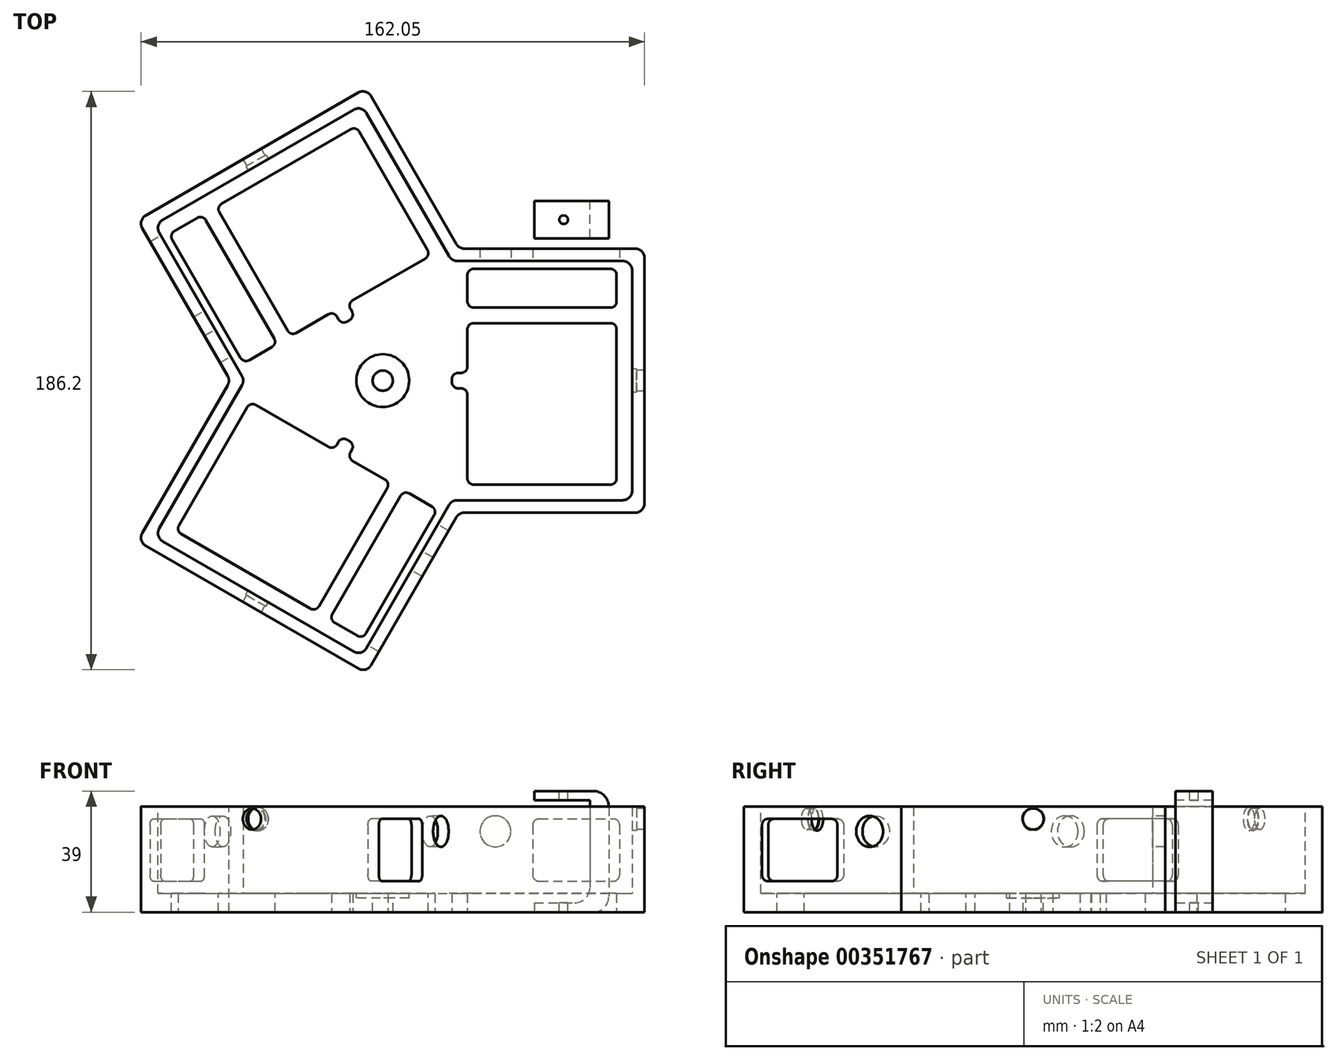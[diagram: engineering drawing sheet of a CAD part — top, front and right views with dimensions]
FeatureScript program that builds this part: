
annotation { "Feature Type Name" : "Feature", "Feature Type Description" : "" }
export const myFeature = defineFeature(function(context is Context, id is Id, definition is map)
    precondition{}
    {
        {
            var Q0;
            Q0=qCreatedBy(makeId("Top.planeOp"),FACE);
            var sketch = newSketch(context, id + "F0", { "sketchPlane" : qUnion([Q0])});
            skCircle(sketch, "E0.cCircle", {"center": v(0, 0) * mm, "radius": 22.23 * mm, "construction": true});
            skLineSegment(sketch, "E0.0", {"start": v(22.23, 38.5) * mm, "end": v(22.23, -38.5) * mm});
            skLineSegment(sketch, "E0.1", {"start": v(22.23, -38.5) * mm, "end": v(-44.46, 0) * mm});
            skLineSegment(sketch, "E0.2", {"start": v(-44.46, 0) * mm, "end": v(22.23, 38.5) * mm});
            skPoint(sketch, "E0.0.midPoint", {"position": v(22.23, 0) * mm});
            skLineSegment(sketch, "E1.bottom", {"start": v(22.23, 38.5) * mm, "end": v(80.23, 38.5) * mm});
            skLineSegment(sketch, "E1.top", {"start": v(22.23, -38.5) * mm, "end": v(80.23, -38.5) * mm});
            skLineSegment(sketch, "E1.right", {"start": v(80.23, 38.5) * mm, "end": v(80.23, -38.5) * mm});
            skLineSegment(sketch, "E2", {"start": v(22.23, 38.5) * mm, "end": v(-6.77, 88.73) * mm});
            skLineSegment(sketch, "E3", {"start": v(-6.77, 88.73) * mm, "end": v(-73.46, 50.23) * mm});
            skLineSegment(sketch, "E4", {"start": v(-73.46, 50.23) * mm, "end": v(-44.46, 0) * mm});
            skLineSegment(sketch, "E5", {"start": v(-44.46, 0) * mm, "end": v(-73.46, -50.23) * mm});
            skLineSegment(sketch, "E6", {"start": v(-73.46, -50.23) * mm, "end": v(-6.77, -88.73) * mm});
            skLineSegment(sketch, "E7", {"start": v(-6.77, -88.73) * mm, "end": v(22.23, -38.5) * mm});
            skLineSegment(sketch, "E8.0", {"start": v(24.54, 42.5) * mm, "end": v(-5.3, 94.2) * mm});
            skLineSegment(sketch, "E8.1", {"start": v(-5.3, 94.2) * mm, "end": v(-78.92, 51.7) * mm});
            skLineSegment(sketch, "E8.2", {"start": v(24.54, 42.5) * mm, "end": v(84.23, 42.5) * mm});
            skLineSegment(sketch, "E8.3", {"start": v(-78.92, 51.7) * mm, "end": v(-49.07, 0) * mm});
            skLineSegment(sketch, "E8.4", {"start": v(-49.07, 0) * mm, "end": v(-78.92, -51.7) * mm});
            skLineSegment(sketch, "E8.5", {"start": v(84.23, 42.5) * mm, "end": v(84.23, -42.5) * mm});
            skLineSegment(sketch, "E8.6", {"start": v(24.54, -42.5) * mm, "end": v(84.23, -42.5) * mm});
            skLineSegment(sketch, "E8.7", {"start": v(-5.3, -94.2) * mm, "end": v(24.54, -42.5) * mm});
            skLineSegment(sketch, "E8.8", {"start": v(-78.92, -51.7) * mm, "end": v(-5.3, -94.2) * mm});
            skLineSegment(sketch, "E9.bottom", {"start": v(75.23, 23.5) * mm, "end": v(27.23, 23.5) * mm});
            skLineSegment(sketch, "E9.top", {"start": v(75.23, 36) * mm, "end": v(27.23, 36) * mm});
            skLineSegment(sketch, "E9.left", {"start": v(75.23, 23.5) * mm, "end": v(75.23, 36) * mm});
            skLineSegment(sketch, "E9.right", {"start": v(27.23, 23.5) * mm, "end": v(27.23, 36) * mm});
            skPoint(sketch, "E9.middle", {"position": v(51.23, 29.75) * mm});
            skPoint(sketch, "E9.middle.positionSnap0", {"position": v(51.23, 38.5) * mm});
            skPoint(sketch, "E9.centerSnap0", {"position": v(51.23, 38.5) * mm});
            skLineSegment(sketch, "E10.1.0", {"start": v(-57.97, 53.4) * mm, "end": v(-33.97, 11.83) * mm});
            skLineSegment(sketch, "E10.1.1", {"start": v(-33.97, 11.83) * mm, "end": v(-44.8, 5.58) * mm});
            skLineSegment(sketch, "E10.1.2", {"start": v(-68.8, 47.15) * mm, "end": v(-44.8, 5.58) * mm});
            skLineSegment(sketch, "E10.1.3", {"start": v(-57.97, 53.4) * mm, "end": v(-68.8, 47.15) * mm});
            skLineSegment(sketch, "E10.2.0", {"start": v(-17.26, -76.9) * mm, "end": v(6.74, -35.33) * mm});
            skLineSegment(sketch, "E10.2.1", {"start": v(6.74, -35.33) * mm, "end": v(17.56, -41.58) * mm});
            skLineSegment(sketch, "E10.2.2", {"start": v(-6.44, -83.15) * mm, "end": v(17.56, -41.58) * mm});
            skLineSegment(sketch, "E10.2.3", {"start": v(-17.26, -76.9) * mm, "end": v(-6.44, -83.15) * mm});
            skLineSegment(sketch, "E11.bottom", {"start": v(22.23, -2.5) * mm, "end": v(27.23, -2.5) * mm});
            skLineSegment(sketch, "E11.top", {"start": v(22.23, 2.5) * mm, "end": v(27.23, 2.5) * mm});
            skLineSegment(sketch, "E11.left", {"start": v(22.23, -2.5) * mm, "end": v(22.23, 2.5) * mm});
            skLineSegment(sketch, "E11.right", {"start": v(27.23, -2.5) * mm, "end": v(27.23, 2.5) * mm});
            skPoint(sketch, "E11.middle", {"position": v(24.73, 0) * mm});
            skLineSegment(sketch, "E12.1.0", {"start": v(-13.28, 18) * mm, "end": v(-15.78, 22.33) * mm});
            skLineSegment(sketch, "E12.1.1", {"start": v(-11.45, 24.83) * mm, "end": v(-15.78, 22.33) * mm});
            skLineSegment(sketch, "E12.1.2", {"start": v(-8.95, 20.5) * mm, "end": v(-11.45, 24.83) * mm});
            skLineSegment(sketch, "E12.2.0", {"start": v(-8.95, -20.5) * mm, "end": v(-11.45, -24.83) * mm});
            skLineSegment(sketch, "E12.2.1", {"start": v(-15.78, -22.33) * mm, "end": v(-11.45, -24.83) * mm});
            skLineSegment(sketch, "E12.2.2", {"start": v(-13.28, -18) * mm, "end": v(-15.78, -22.33) * mm});
            skLineSegment(sketch, "E13.bottom", {"start": v(75.23, -33.5) * mm, "end": v(27.23, -33.5) * mm});
            skLineSegment(sketch, "E13.top", {"start": v(75.23, 18.5) * mm, "end": v(27.23, 18.5) * mm});
            skLineSegment(sketch, "E13.left", {"start": v(75.23, -33.5) * mm, "end": v(75.23, 18.5) * mm});
            skLineSegment(sketch, "E13.right", {"start": v(27.23, -33.5) * mm, "end": v(27.23, 18.5) * mm});
            skPoint(sketch, "E13.middle", {"position": v(51.23, 0) * mm});
            skPoint(sketch, "E13.middle.positionSnap0", {"position": v(51.23, 23.5) * mm});
            skPoint(sketch, "E13.centerSnap0", {"position": v(51.23, 23.5) * mm});
            skLineSegment(sketch, "E14.1.0", {"start": v(-8.6, 81.9) * mm, "end": v(-53.64, 55.9) * mm});
            skLineSegment(sketch, "E14.1.1", {"start": v(15.4, 40.33) * mm, "end": v(-29.64, 14.33) * mm});
            skLineSegment(sketch, "E14.1.2", {"start": v(-53.64, 55.9) * mm, "end": v(-29.64, 14.33) * mm});
            skLineSegment(sketch, "E14.1.3", {"start": v(-8.6, 81.9) * mm, "end": v(15.4, 40.33) * mm});
            skLineSegment(sketch, "E14.2.0", {"start": v(-66.63, -48.4) * mm, "end": v(-21.6, -74.4) * mm});
            skLineSegment(sketch, "E14.2.1", {"start": v(-42.63, -6.83) * mm, "end": v(2.4, -32.83) * mm});
            skLineSegment(sketch, "E14.2.2", {"start": v(-21.6, -74.4) * mm, "end": v(2.4, -32.83) * mm});
            skLineSegment(sketch, "E14.2.3", {"start": v(-66.63, -48.4) * mm, "end": v(-42.63, -6.83) * mm});
            skSolve(sketch);
        }
        {
            var Q0;
            Q0 = qSketchRegion(id + "F0", true);
            extrude(context, id + "F1", {"entities" : qUnion([Q0]), "depth" : 34 * mm, "offsetDistance" : 25 * mm});
        }
        {
            var Q0;
            Q0=makeQuery(id+"F0.imprint","IMPRINT",FACE,{"disambiguationData":[TD([[makeQuery(id+"F0.imprint","IMPRINT",EDGE,{"derivedFrom":sQuery(id+"F0.wireOp",EDGE,"E0.2")}),1.0]])]});
            var Q1;
            Q1=makeQuery(id+"F0.imprint","IMPRINT",FACE,{"disambiguationData":[TD([[makeQuery(id+"F0.imprint","IMPRINT",EDGE,{"derivedFrom":sQuery(id+"F0.wireOp",EDGE,"E0.1")}),-1.0]])]});
            var Q2;
            Q2=makeQuery(id+"F0.imprint","IMPRINT",FACE,{"disambiguationData":[TD([[makeQuery(id+"F0.imprint","IMPRINT",EDGE,{"derivedFrom":sQuery(id+"F0.wireOp",EDGE,"E0.1")}),1.0]])]});
            var Q3;
            Q3=makeQuery(id+"F0.imprint","IMPRINT",FACE,{"disambiguationData":[TD([[makeQuery(id+"F0.imprint","IMPRINT",EDGE,{"derivedFrom":sQuery(id+"F0.wireOp",EDGE,"E1.bottom")}),-1.0]])]});
            var Q4;
            Q4=makeQuery(id+"F0.imprint","IMPRINT",FACE,{"disambiguationData":[TD([[makeQuery(id+"F0.imprint","IMPRINT",EDGE,{"derivedFrom":sQuery(id+"F0.wireOp",EDGE,"E1.bottom")}),1.0]])]});
            extrude(context, id + "F2", {"entities" : qUnion([Q0, Q1, Q2, Q3, Q4]), "operationType" : NewBodyOperationType.ADD, "depth" : 6 * mm, "offsetDistance" : 25 * mm});
        }
        {
            var Q0;
            Q0=makeQuery(id+"F1.opExtrude","SWEPT_FACE",FACE,{"disambiguationData":[OSD([sQuery(id+"F0.wireOp",EDGE,"E6")])]});
            var sketch = newSketch(context, id + "F3", { "sketchPlane" : qUnion([Q0])});
            skCircle(sketch, "E15", {"center": v(0, 30) * mm, "radius": 5.25 * mm});
            skPoint(sketch, "E15.centerSnap0", {"position": v(0, 34) * mm});
            skSolve(sketch);
        }
        {
            var Q0;
            Q0=makeQuery(id+"F1.opExtrude","SWEPT_FACE",FACE,{"disambiguationData":[OSD([sQuery(id+"F0.wireOp",EDGE,"E3")])]});
            var sketch = newSketch(context, id + "F4", { "sketchPlane" : qUnion([Q0])});
            skCircle(sketch, "E16", {"center": v(0, 30) * mm, "radius": 3.58 * mm});
            skPoint(sketch, "E16.centerSnap0", {"position": v(0, 34) * mm});
            skSolve(sketch);
        }
        {
            var Q0;
            Q0=makeQuery(id+"F1.opExtrude","SWEPT_FACE",FACE,{"disambiguationData":[OSD([sQuery(id+"F0.wireOp",EDGE,"E1.right")])]});
            var sketch = newSketch(context, id + "F5", { "sketchPlane" : qUnion([Q0])});
            skCircle(sketch, "E17", {"center": v(0, 30) * mm, "radius": 4.93 * mm});
            skPoint(sketch, "E17.centerSnap0", {"position": v(0, 34) * mm});
            skSolve(sketch);
        }
        {
            var Q0;
            Q0=sQuery(id+"F4.wireOp",VERTEX,"E16.center");
            var Q1;
            Q1=sQuery(id+"F5.wireOp",VERTEX,"E17.center");
            var Q2;
            Q2=sQuery(id+"F3.wireOp",VERTEX,"E15.center");
            var Q3;
            Q3=makeQuery(id+"F1.opExtrude","SWEPT_BODY",BODY,{"disambiguationData":[OSD([sQuery(id+"F0.wireOp",EDGE,"E1.bottom"),sQuery(id+"F0.wireOp",EDGE,"E1.top"),sQuery(id+"F0.wireOp",EDGE,"E1.right"),sQuery(id+"F0.wireOp",EDGE,"E2"),sQuery(id+"F0.wireOp",EDGE,"E3"),sQuery(id+"F0.wireOp",EDGE,"E4"),sQuery(id+"F0.wireOp",EDGE,"E5"),sQuery(id+"F0.wireOp",EDGE,"E6"),sQuery(id+"F0.wireOp",EDGE,"E7"),sQuery(id+"F0.wireOp",EDGE,"E8.0"),sQuery(id+"F0.wireOp",EDGE,"E8.1"),sQuery(id+"F0.wireOp",EDGE,"E8.2"),sQuery(id+"F0.wireOp",EDGE,"E8.3"),sQuery(id+"F0.wireOp",EDGE,"E8.4"),sQuery(id+"F0.wireOp",EDGE,"E8.5"),sQuery(id+"F0.wireOp",EDGE,"E8.6"),sQuery(id+"F0.wireOp",EDGE,"E8.7"),sQuery(id+"F0.wireOp",EDGE,"E8.8")])]});
            hole(context, id + "F6", {"style" : HoleStyle.C_BORE, "endStyle" : HoleEndStyle.BLIND, "holeDiameter" : 6.8 * mm, "cBoreDiameter" : 7.5 * mm, "cBoreDepth" : 1.5 * mm, "majorDiameter" : 5 * mm, "holeDepth" : 6 * mm, "isTappedThrough" : true, "tappedDepth" : 12 * mm, "tapClearance" : 3, "locations" : qUnion([Q0, Q1, Q2]), "scope" : qUnion([Q3])});
        }
        {
            var Q0;
            Q0=makeQuery(id+"F1.opExtrude","SWEPT_FACE",FACE,{"disambiguationData":[OSD([sQuery(id+"F0.wireOp",EDGE,"E7")])]});
            var sketch = newSketch(context, id + "F7", { "sketchPlane" : qUnion([Q0])});
            skCircle(sketch, "E18", {"center": v(36.23, 26) * mm, "radius": 6.66 * mm});
            skLineSegment(sketch, "E19.bottom", {"start": v(48.23, 30) * mm, "end": v(76.23, 30) * mm});
            skLineSegment(sketch, "E19.top", {"start": v(48.23, 10) * mm, "end": v(76.23, 10) * mm});
            skLineSegment(sketch, "E19.left", {"start": v(48.23, 30) * mm, "end": v(48.23, 10) * mm});
            skLineSegment(sketch, "E19.right", {"start": v(76.23, 30) * mm, "end": v(76.23, 10) * mm});
            skSolve(sketch);
        }
        {
            var Q0;
            Q0=makeQuery(id+"F1.opExtrude","SWEPT_FACE",FACE,{"disambiguationData":[OSD([sQuery(id+"F0.wireOp",EDGE,"E1.bottom")])]});
            var sketch = newSketch(context, id + "F8", { "sketchPlane" : qUnion([Q0])});
            skCircle(sketch, "E20", {"center": v(36.23, 26) * mm, "radius": 5.26 * mm});
            skLineSegment(sketch, "E21.bottom", {"start": v(48.23, 30) * mm, "end": v(76.23, 30) * mm});
            skLineSegment(sketch, "E21.top", {"start": v(48.23, 10) * mm, "end": v(76.23, 10) * mm});
            skLineSegment(sketch, "E21.left", {"start": v(48.23, 30) * mm, "end": v(48.23, 10) * mm});
            skLineSegment(sketch, "E21.right", {"start": v(76.23, 30) * mm, "end": v(76.23, 10) * mm});
            skSolve(sketch);
        }
        {
            var Q0;
            Q0=makeQuery(id+"F1.opExtrude","SWEPT_FACE",FACE,{"disambiguationData":[OSD([sQuery(id+"F0.wireOp",EDGE,"E4")])]});
            var sketch = newSketch(context, id + "F9", { "sketchPlane" : qUnion([Q0])});
            skCircle(sketch, "E22", {"center": v(36.23, 26) * mm, "radius": 7.55 * mm});
            skLineSegment(sketch, "E23.bottom", {"start": v(76.23, 30) * mm, "end": v(48.23, 30) * mm});
            skLineSegment(sketch, "E23.top", {"start": v(76.23, 10) * mm, "end": v(48.23, 10) * mm});
            skLineSegment(sketch, "E23.left", {"start": v(76.23, 30) * mm, "end": v(76.23, 10) * mm});
            skLineSegment(sketch, "E23.right", {"start": v(48.23, 30) * mm, "end": v(48.23, 10) * mm});
            skSolve(sketch);
        }
        {
            var Q0;
            Q0=sQuery(id+"F8.wireOp",VERTEX,"E20.center");
            var Q1;
            Q1=sQuery(id+"F9.wireOp",VERTEX,"E22.center");
            var Q2;
            Q2=sQuery(id+"F7.wireOp",VERTEX,"E18.center");
            var Q3;
            Q3=makeQuery(id+"F1.opExtrude","SWEPT_BODY",BODY,{"disambiguationData":[OSD([sQuery(id+"F0.wireOp",EDGE,"E1.bottom"),sQuery(id+"F0.wireOp",EDGE,"E1.top"),sQuery(id+"F0.wireOp",EDGE,"E1.right"),sQuery(id+"F0.wireOp",EDGE,"E2"),sQuery(id+"F0.wireOp",EDGE,"E3"),sQuery(id+"F0.wireOp",EDGE,"E4"),sQuery(id+"F0.wireOp",EDGE,"E5"),sQuery(id+"F0.wireOp",EDGE,"E6"),sQuery(id+"F0.wireOp",EDGE,"E7"),sQuery(id+"F0.wireOp",EDGE,"E8.0"),sQuery(id+"F0.wireOp",EDGE,"E8.1"),sQuery(id+"F0.wireOp",EDGE,"E8.2"),sQuery(id+"F0.wireOp",EDGE,"E8.3"),sQuery(id+"F0.wireOp",EDGE,"E8.4"),sQuery(id+"F0.wireOp",EDGE,"E8.5"),sQuery(id+"F0.wireOp",EDGE,"E8.6"),sQuery(id+"F0.wireOp",EDGE,"E8.7"),sQuery(id+"F0.wireOp",EDGE,"E8.8")])]});
            hole(context, id + "F10", {"style" : HoleStyle.SIMPLE, "endStyle" : HoleEndStyle.BLIND, "holeDiameter" : 10 * mm, "majorDiameter" : 5 * mm, "holeDepth" : 6 * mm, "isTappedThrough" : true, "tappedDepth" : 12 * mm, "tapClearance" : 3, "locations" : qUnion([Q0, Q1, Q2]), "scope" : qUnion([Q3])});
        }
        {
            var Q0;
            Q0=makeQuery(id+"F9.imprint","IMPRINT",FACE,{"disambiguationData":[TD([[makeQuery(id+"F9.imprint","IMPRINT",EDGE,{"derivedFrom":sQuery(id+"F9.wireOp",EDGE,"E23.bottom")}),1.0]])]});
            extrude(context, id + "F11", {"entities" : qUnion([Q0]), "operationType" : NewBodyOperationType.REMOVE, "oppositeDirection" : true, "depth" : 25 * mm, "offsetDistance" : 25 * mm});
        }
        {
            var Q0;
            Q0=makeQuery(id+"F7.imprint","IMPRINT",FACE,{"disambiguationData":[TD([[makeQuery(id+"F7.imprint","IMPRINT",EDGE,{"derivedFrom":sQuery(id+"F7.wireOp",EDGE,"E19.bottom")}),-1.0]])]});
            extrude(context, id + "F12", {"entities" : qUnion([Q0]), "operationType" : NewBodyOperationType.REMOVE, "oppositeDirection" : true, "depth" : 25 * mm, "offsetDistance" : 25 * mm});
        }
        {
            var Q0;
            Q0=makeQuery(id+"F8.imprint","IMPRINT",FACE,{"disambiguationData":[TD([[makeQuery(id+"F8.imprint","IMPRINT",EDGE,{"derivedFrom":sQuery(id+"F8.wireOp",EDGE,"E21.bottom")}),-1.0]])]});
            extrude(context, id + "F13", {"entities" : qUnion([Q0]), "operationType" : NewBodyOperationType.REMOVE, "oppositeDirection" : true, "depth" : 25 * mm, "offsetDistance" : 25 * mm});
        }
        {
            var Q0;
            Q0=makeQuery(id+"F2.opExtrude","CAP_FACE",FACE,{"disambiguationData":[OSD([sQuery(id+"F0.wireOp",EDGE,"E8.0"),sQuery(id+"F0.wireOp",EDGE,"E8.1"),sQuery(id+"F0.wireOp",EDGE,"E8.2"),sQuery(id+"F0.wireOp",EDGE,"E8.3"),sQuery(id+"F0.wireOp",EDGE,"E8.4"),sQuery(id+"F0.wireOp",EDGE,"E8.5"),sQuery(id+"F0.wireOp",EDGE,"E8.6"),sQuery(id+"F0.wireOp",EDGE,"E8.7"),sQuery(id+"F0.wireOp",EDGE,"E8.8")])],"isStart":false});
            var sketch = newSketch(context, id + "F14", { "sketchPlane" : qUnion([Q0])});
            skCircle(sketch, "E24", {"center": v(0, 0) * mm, "radius": 9.97 * mm});
            skSolve(sketch);
        }
        {
            var Q0;
            Q0=sQuery(id+"F14.wireOp",VERTEX,"E24.center");
            var Q1;
            Q1=makeQuery(id+"F1.opExtrude","SWEPT_BODY",BODY,{"disambiguationData":[OSD([sQuery(id+"F0.wireOp",EDGE,"E1.bottom"),sQuery(id+"F0.wireOp",EDGE,"E1.top"),sQuery(id+"F0.wireOp",EDGE,"E1.right"),sQuery(id+"F0.wireOp",EDGE,"E2"),sQuery(id+"F0.wireOp",EDGE,"E3"),sQuery(id+"F0.wireOp",EDGE,"E4"),sQuery(id+"F0.wireOp",EDGE,"E5"),sQuery(id+"F0.wireOp",EDGE,"E6"),sQuery(id+"F0.wireOp",EDGE,"E7"),sQuery(id+"F0.wireOp",EDGE,"E8.0"),sQuery(id+"F0.wireOp",EDGE,"E8.1"),sQuery(id+"F0.wireOp",EDGE,"E8.2"),sQuery(id+"F0.wireOp",EDGE,"E8.3"),sQuery(id+"F0.wireOp",EDGE,"E8.4"),sQuery(id+"F0.wireOp",EDGE,"E8.5"),sQuery(id+"F0.wireOp",EDGE,"E8.6"),sQuery(id+"F0.wireOp",EDGE,"E8.7"),sQuery(id+"F0.wireOp",EDGE,"E8.8")])]});
            hole(context, id + "F15", {"style" : HoleStyle.C_BORE, "endStyle" : HoleEndStyle.THROUGH, "holeDiameter" : 6.5 * mm, "cBoreDiameter" : 17 * mm, "cBoreDepth" : 1.5 * mm, "majorDiameter" : 5 * mm, "isTappedThrough" : true, "tappedDepth" : 12 * mm, "tapClearance" : 3, "locations" : qUnion([Q0]), "scope" : qUnion([Q1])});
        }
        {
            var Q0;
            Q0=makeQuery(id+"F11.boolean.opBoolean","COPY",EDGE,{"derivedFrom":makeQuery(id+"F11.opExtrude","SWEPT_EDGE",EDGE,{"disambiguationData":[OSD([sQuery(id+"F9.wireOp",EDGE,"E23.bottom"),sQuery(id+"F9.wireOp",EDGE,"E23.left")])]})});
            var Q1;
            Q1=makeQuery(id+"F11.boolean.opBoolean","COPY",EDGE,{"derivedFrom":makeQuery(id+"F11.opExtrude","SWEPT_EDGE",EDGE,{"disambiguationData":[OSD([sQuery(id+"F9.wireOp",EDGE,"E23.bottom"),sQuery(id+"F9.wireOp",EDGE,"E23.right")])]})});
            var Q2;
            Q2=makeQuery(id+"F11.boolean.opBoolean","COPY",EDGE,{"derivedFrom":makeQuery(id+"F11.opExtrude","SWEPT_EDGE",EDGE,{"disambiguationData":[OSD([sQuery(id+"F9.wireOp",EDGE,"E23.top"),sQuery(id+"F9.wireOp",EDGE,"E23.right")])]})});
            var Q3;
            Q3=makeQuery(id+"F11.boolean.opBoolean","COPY",EDGE,{"derivedFrom":makeQuery(id+"F11.opExtrude","SWEPT_EDGE",EDGE,{"disambiguationData":[OSD([sQuery(id+"F9.wireOp",EDGE,"E23.top"),sQuery(id+"F9.wireOp",EDGE,"E23.left")])]})});
            var Q4;
            Q4=makeQuery(id+"F12.boolean.opBoolean","COPY",EDGE,{"derivedFrom":makeQuery(id+"F12.opExtrude","SWEPT_EDGE",EDGE,{"disambiguationData":[OSD([sQuery(id+"F7.wireOp",EDGE,"E19.bottom"),sQuery(id+"F7.wireOp",EDGE,"E19.right")])]})});
            var Q5;
            Q5=makeQuery(id+"F12.boolean.opBoolean","COPY",EDGE,{"derivedFrom":makeQuery(id+"F12.opExtrude","SWEPT_EDGE",EDGE,{"disambiguationData":[OSD([sQuery(id+"F7.wireOp",EDGE,"E19.bottom"),sQuery(id+"F7.wireOp",EDGE,"E19.left")])]})});
            var Q6;
            Q6=makeQuery(id+"F12.boolean.opBoolean","COPY",EDGE,{"derivedFrom":makeQuery(id+"F12.opExtrude","SWEPT_EDGE",EDGE,{"disambiguationData":[OSD([sQuery(id+"F7.wireOp",EDGE,"E19.top"),sQuery(id+"F7.wireOp",EDGE,"E19.left")])]})});
            var Q7;
            Q7=makeQuery(id+"F12.boolean.opBoolean","COPY",EDGE,{"derivedFrom":makeQuery(id+"F12.opExtrude","SWEPT_EDGE",EDGE,{"disambiguationData":[OSD([sQuery(id+"F7.wireOp",EDGE,"E19.top"),sQuery(id+"F7.wireOp",EDGE,"E19.right")])]})});
            var Q8;
            Q8=makeQuery(id+"F13.boolean.opBoolean","COPY",EDGE,{"derivedFrom":makeQuery(id+"F13.opExtrude","SWEPT_EDGE",EDGE,{"disambiguationData":[OSD([sQuery(id+"F8.wireOp",EDGE,"E21.top"),sQuery(id+"F8.wireOp",EDGE,"E21.right")])]})});
            var Q9;
            Q9=makeQuery(id+"F13.boolean.opBoolean","COPY",EDGE,{"derivedFrom":makeQuery(id+"F13.opExtrude","SWEPT_EDGE",EDGE,{"disambiguationData":[OSD([sQuery(id+"F8.wireOp",EDGE,"E21.bottom"),sQuery(id+"F8.wireOp",EDGE,"E21.right")])]})});
            var Q10;
            Q10=makeQuery(id+"F13.boolean.opBoolean","COPY",EDGE,{"derivedFrom":makeQuery(id+"F13.opExtrude","SWEPT_EDGE",EDGE,{"disambiguationData":[OSD([sQuery(id+"F8.wireOp",EDGE,"E21.bottom"),sQuery(id+"F8.wireOp",EDGE,"E21.left")])]})});
            var Q11;
            Q11=makeQuery(id+"F13.boolean.opBoolean","COPY",EDGE,{"derivedFrom":makeQuery(id+"F13.opExtrude","SWEPT_EDGE",EDGE,{"disambiguationData":[OSD([sQuery(id+"F8.wireOp",EDGE,"E21.top"),sQuery(id+"F8.wireOp",EDGE,"E21.left")])]})});
            fillet(context, id + "F16", {"entities" : qUnion([Q0, Q1, Q2, Q3, Q4, Q5, Q6, Q7, Q8, Q9, Q10, Q11]), "radius" : 2 * mm, "tangentPropagation" : true, "allowEdgeOverflow" : false});
        }
        {
            var Q0;
            Q0=makeQuery(id+"F2.opExtrude","SWEPT_EDGE",EDGE,{"disambiguationData":[OSD([sQuery(id+"F0.wireOp",EDGE,"E10.2.2"),sQuery(id+"F0.wireOp",EDGE,"E10.2.3")])]});
            var Q1;
            Q1=makeQuery(id+"F2.opExtrude","SWEPT_EDGE",EDGE,{"disambiguationData":[OSD([sQuery(id+"F0.wireOp",EDGE,"E10.2.1"),sQuery(id+"F0.wireOp",EDGE,"E10.2.2")])]});
            var Q2;
            Q2=makeQuery(id+"F2.opExtrude","SWEPT_EDGE",EDGE,{"disambiguationData":[OSD([sQuery(id+"F0.wireOp",EDGE,"E10.2.0"),sQuery(id+"F0.wireOp",EDGE,"E10.2.1")])]});
            var Q3;
            Q3=makeQuery(id+"F2.opExtrude","SWEPT_EDGE",EDGE,{"disambiguationData":[OSD([sQuery(id+"F0.wireOp",EDGE,"E10.2.0"),sQuery(id+"F0.wireOp",EDGE,"E10.2.3")])]});
            var Q4;
            Q4=makeQuery(id+"F2.opExtrude","SWEPT_EDGE",EDGE,{"disambiguationData":[OSD([sQuery(id+"F0.wireOp",EDGE,"E14.2.0"),sQuery(id+"F0.wireOp",EDGE,"E14.2.2")])]});
            var Q5;
            Q5=makeQuery(id+"F2.opExtrude","SWEPT_EDGE",EDGE,{"disambiguationData":[OSD([sQuery(id+"F0.wireOp",EDGE,"E14.2.0"),sQuery(id+"F0.wireOp",EDGE,"E14.2.3")])]});
            var Q6;
            Q6=makeQuery(id+"F2.opExtrude","SWEPT_EDGE",EDGE,{"disambiguationData":[OSD([sQuery(id+"F0.wireOp",EDGE,"E14.2.1"),sQuery(id+"F0.wireOp",EDGE,"E14.2.3")])]});
            var Q7;
            Q7=makeQuery(id+"F2.opExtrude","SWEPT_EDGE",EDGE,{"disambiguationData":[OSD([sQuery(id+"F0.wireOp",EDGE,"E12.2.0"),sQuery(id+"F0.wireOp",EDGE,"E14.2.1")])]});
            var Q8;
            Q8=makeQuery(id+"F2.opExtrude","SWEPT_EDGE",EDGE,{"disambiguationData":[OSD([sQuery(id+"F0.wireOp",EDGE,"E12.2.2"),sQuery(id+"F0.wireOp",EDGE,"E14.2.1")])]});
            var Q9;
            Q9=makeQuery(id+"F2.opExtrude","SWEPT_EDGE",EDGE,{"disambiguationData":[OSD([sQuery(id+"F0.wireOp",EDGE,"E0.1"),sQuery(id+"F0.wireOp",EDGE,"E12.2.0")])]});
            var Q10;
            Q10=makeQuery(id+"F2.opExtrude","SWEPT_EDGE",EDGE,{"disambiguationData":[OSD([sQuery(id+"F0.wireOp",EDGE,"E0.1"),sQuery(id+"F0.wireOp",EDGE,"E12.2.2")])]});
            var Q11;
            Q11=makeQuery(id+"F2.opExtrude","SWEPT_EDGE",EDGE,{"disambiguationData":[OSD([sQuery(id+"F0.wireOp",EDGE,"E14.2.1"),sQuery(id+"F0.wireOp",EDGE,"E14.2.2")])]});
            var Q12;
            Q12=makeQuery(id+"F2.opExtrude","SWEPT_EDGE",EDGE,{"disambiguationData":[OSD([sQuery(id+"F0.wireOp",EDGE,"E14.2.1"),sQuery(id+"F0.wireOp",EDGE,"E14.2.2")])]});
            var Q13;
            Q13=makeQuery(id+"F2.opExtrude","SWEPT_EDGE",EDGE,{"disambiguationData":[OSD([sQuery(id+"F0.wireOp",EDGE,"E12.2.0"),sQuery(id+"F0.wireOp",EDGE,"E14.2.1")])]});
            var Q14;
            Q14=makeQuery(id+"F2.opExtrude","SWEPT_EDGE",EDGE,{"disambiguationData":[OSD([sQuery(id+"F0.wireOp",EDGE,"E0.1"),sQuery(id+"F0.wireOp",EDGE,"E12.2.0")])]});
            var Q15;
            Q15=makeQuery(id+"F2.opExtrude","SWEPT_EDGE",EDGE,{"disambiguationData":[OSD([sQuery(id+"F0.wireOp",EDGE,"E12.2.2"),sQuery(id+"F0.wireOp",EDGE,"E14.2.1")])]});
            var Q16;
            Q16=makeQuery(id+"F2.opExtrude","SWEPT_EDGE",EDGE,{"disambiguationData":[OSD([sQuery(id+"F0.wireOp",EDGE,"E0.1"),sQuery(id+"F0.wireOp",EDGE,"E12.2.2")])]});
            var Q17;
            Q17=makeQuery(id+"F2.opExtrude","SWEPT_EDGE",EDGE,{"disambiguationData":[OSD([sQuery(id+"F0.wireOp",EDGE,"E10.2.0"),sQuery(id+"F0.wireOp",EDGE,"E10.2.1")])]});
            var Q18;
            Q18=makeQuery(id+"F2.opExtrude","SWEPT_EDGE",EDGE,{"disambiguationData":[OSD([sQuery(id+"F0.wireOp",EDGE,"E10.2.1"),sQuery(id+"F0.wireOp",EDGE,"E10.2.2")])]});
            var Q19;
            Q19=makeQuery(id+"F2.opExtrude","SWEPT_EDGE",EDGE,{"disambiguationData":[OSD([sQuery(id+"F0.wireOp",EDGE,"E10.2.2"),sQuery(id+"F0.wireOp",EDGE,"E10.2.3")])]});
            var Q20;
            Q20=makeQuery(id+"F2.opExtrude","SWEPT_EDGE",EDGE,{"disambiguationData":[OSD([sQuery(id+"F0.wireOp",EDGE,"E14.2.0"),sQuery(id+"F0.wireOp",EDGE,"E14.2.2")])]});
            var Q21;
            Q21=makeQuery(id+"F2.opExtrude","SWEPT_EDGE",EDGE,{"disambiguationData":[OSD([sQuery(id+"F0.wireOp",EDGE,"E10.2.0"),sQuery(id+"F0.wireOp",EDGE,"E10.2.3")])]});
            var Q22;
            Q22=makeQuery(id+"F2.opExtrude","SWEPT_EDGE",EDGE,{"disambiguationData":[OSD([sQuery(id+"F0.wireOp",EDGE,"E14.2.0"),sQuery(id+"F0.wireOp",EDGE,"E14.2.3")])]});
            var Q23;
            Q23=makeQuery(id+"F2.opExtrude","SWEPT_EDGE",EDGE,{"disambiguationData":[OSD([sQuery(id+"F0.wireOp",EDGE,"E14.2.1"),sQuery(id+"F0.wireOp",EDGE,"E14.2.3")])]});
            fillet(context, id + "F17", {"entities" : qUnion([Q0, Q1, Q2, Q3, Q4, Q5, Q6, Q7, Q8, Q9, Q10, Q11, Q12, Q13, Q14, Q15, Q16, Q17, Q18, Q19, Q20, Q21, Q22, Q23]), "radius" : 2 * mm, "tangentPropagation" : true, "allowEdgeOverflow" : false});
        }
        {
            var Q0;
            Q0=makeQuery(id+"F2.opExtrude","SWEPT_EDGE",EDGE,{"disambiguationData":[OSD([sQuery(id+"F0.wireOp",EDGE,"E10.1.1"),sQuery(id+"F0.wireOp",EDGE,"E10.1.2")])]});
            var Q1;
            Q1=makeQuery(id+"F2.opExtrude","SWEPT_EDGE",EDGE,{"disambiguationData":[OSD([sQuery(id+"F0.wireOp",EDGE,"E14.1.1"),sQuery(id+"F0.wireOp",EDGE,"E14.1.2")])]});
            var Q2;
            Q2=makeQuery(id+"F2.opExtrude","SWEPT_EDGE",EDGE,{"disambiguationData":[OSD([sQuery(id+"F0.wireOp",EDGE,"E10.1.0"),sQuery(id+"F0.wireOp",EDGE,"E10.1.1")])]});
            var Q3;
            Q3=makeQuery(id+"F2.opExtrude","SWEPT_EDGE",EDGE,{"disambiguationData":[OSD([sQuery(id+"F0.wireOp",EDGE,"E12.1.2"),sQuery(id+"F0.wireOp",EDGE,"E14.1.1")])]});
            var Q4;
            Q4=makeQuery(id+"F2.opExtrude","SWEPT_EDGE",EDGE,{"disambiguationData":[OSD([sQuery(id+"F0.wireOp",EDGE,"E0.2"),sQuery(id+"F0.wireOp",EDGE,"E12.1.2")])]});
            var Q5;
            Q5=makeQuery(id+"F2.opExtrude","SWEPT_EDGE",EDGE,{"disambiguationData":[OSD([sQuery(id+"F0.wireOp",EDGE,"E0.2"),sQuery(id+"F0.wireOp",EDGE,"E12.1.0")])]});
            var Q6;
            Q6=makeQuery(id+"F2.opExtrude","SWEPT_EDGE",EDGE,{"disambiguationData":[OSD([sQuery(id+"F0.wireOp",EDGE,"E12.1.0"),sQuery(id+"F0.wireOp",EDGE,"E14.1.1")])]});
            var Q7;
            Q7=makeQuery(id+"F2.opExtrude","SWEPT_EDGE",EDGE,{"disambiguationData":[OSD([sQuery(id+"F0.wireOp",EDGE,"E14.1.1"),sQuery(id+"F0.wireOp",EDGE,"E14.1.3")])]});
            var Q8;
            Q8=makeQuery(id+"F2.opExtrude","SWEPT_EDGE",EDGE,{"disambiguationData":[OSD([sQuery(id+"F0.wireOp",EDGE,"E14.1.0"),sQuery(id+"F0.wireOp",EDGE,"E14.1.3")])]});
            var Q9;
            Q9=makeQuery(id+"F2.opExtrude","SWEPT_EDGE",EDGE,{"disambiguationData":[OSD([sQuery(id+"F0.wireOp",EDGE,"E14.1.0"),sQuery(id+"F0.wireOp",EDGE,"E14.1.2")])]});
            var Q10;
            Q10=makeQuery(id+"F2.opExtrude","SWEPT_EDGE",EDGE,{"disambiguationData":[OSD([sQuery(id+"F0.wireOp",EDGE,"E10.1.2"),sQuery(id+"F0.wireOp",EDGE,"E10.1.3")])]});
            var Q11;
            Q11=makeQuery(id+"F2.opExtrude","SWEPT_EDGE",EDGE,{"disambiguationData":[OSD([sQuery(id+"F0.wireOp",EDGE,"E10.1.0"),sQuery(id+"F0.wireOp",EDGE,"E10.1.3")])]});
            fillet(context, id + "F18", {"entities" : qUnion([Q0, Q1, Q2, Q3, Q4, Q5, Q6, Q7, Q8, Q9, Q10, Q11]), "radius" : 2 * mm, "tangentPropagation" : true, "allowEdgeOverflow" : false});
        }
        {
            var Q0;
            Q0=makeQuery(id+"F2.opExtrude","SWEPT_EDGE",EDGE,{"disambiguationData":[OSD([sQuery(id+"F0.wireOp",EDGE,"E13.top"),sQuery(id+"F0.wireOp",EDGE,"E13.right")])]});
            var Q1;
            Q1=makeQuery(id+"F2.opExtrude","SWEPT_EDGE",EDGE,{"disambiguationData":[OSD([sQuery(id+"F0.wireOp",EDGE,"E11.top"),sQuery(id+"F0.wireOp",EDGE,"E13.right")])]});
            var Q2;
            Q2=makeQuery(id+"F2.opExtrude","SWEPT_EDGE",EDGE,{"disambiguationData":[OSD([sQuery(id+"F0.wireOp",EDGE,"E0.0"),sQuery(id+"F0.wireOp",EDGE,"E11.top"),sQuery(id+"F0.wireOp",EDGE,"E11.left")])]});
            var Q3;
            Q3=makeQuery(id+"F2.opExtrude","SWEPT_EDGE",EDGE,{"disambiguationData":[OSD([sQuery(id+"F0.wireOp",EDGE,"E11.bottom"),sQuery(id+"F0.wireOp",EDGE,"E13.right")])]});
            var Q4;
            Q4=makeQuery(id+"F2.opExtrude","SWEPT_EDGE",EDGE,{"disambiguationData":[OSD([sQuery(id+"F0.wireOp",EDGE,"E9.bottom"),sQuery(id+"F0.wireOp",EDGE,"E9.right")])]});
            var Q5;
            Q5=makeQuery(id+"F2.opExtrude","SWEPT_EDGE",EDGE,{"disambiguationData":[OSD([sQuery(id+"F0.wireOp",EDGE,"E9.top"),sQuery(id+"F0.wireOp",EDGE,"E9.right")])]});
            var Q6;
            Q6=makeQuery(id+"F2.opExtrude","SWEPT_EDGE",EDGE,{"disambiguationData":[OSD([sQuery(id+"F0.wireOp",EDGE,"E9.top"),sQuery(id+"F0.wireOp",EDGE,"E9.left")])]});
            var Q7;
            Q7=makeQuery(id+"F2.opExtrude","SWEPT_EDGE",EDGE,{"disambiguationData":[OSD([sQuery(id+"F0.wireOp",EDGE,"E13.top"),sQuery(id+"F0.wireOp",EDGE,"E13.left")])]});
            var Q8;
            Q8=makeQuery(id+"F2.opExtrude","SWEPT_EDGE",EDGE,{"disambiguationData":[OSD([sQuery(id+"F0.wireOp",EDGE,"E9.bottom"),sQuery(id+"F0.wireOp",EDGE,"E9.left")])]});
            var Q9;
            Q9=makeQuery(id+"F2.opExtrude","SWEPT_EDGE",EDGE,{"disambiguationData":[OSD([sQuery(id+"F0.wireOp",EDGE,"E13.bottom"),sQuery(id+"F0.wireOp",EDGE,"E13.left")])]});
            var Q10;
            Q10=makeQuery(id+"F2.opExtrude","SWEPT_EDGE",EDGE,{"disambiguationData":[OSD([sQuery(id+"F0.wireOp",EDGE,"E0.0"),sQuery(id+"F0.wireOp",EDGE,"E11.bottom"),sQuery(id+"F0.wireOp",EDGE,"E11.left")])]});
            var Q11;
            Q11=makeQuery(id+"F2.opExtrude","SWEPT_EDGE",EDGE,{"disambiguationData":[OSD([sQuery(id+"F0.wireOp",EDGE,"E13.bottom"),sQuery(id+"F0.wireOp",EDGE,"E13.right")])]});
            fillet(context, id + "F19", {"entities" : qUnion([Q0, Q1, Q2, Q3, Q4, Q5, Q6, Q7, Q8, Q9, Q10, Q11]), "radius" : 2 * mm, "tangentPropagation" : true, "allowEdgeOverflow" : false});
        }
        {
            var Q0;
            Q0=makeQuery(id+"F1.opExtrude","SWEPT_EDGE",EDGE,{"disambiguationData":[OSD([sQuery(id+"F0.wireOp",EDGE,"E1.bottom"),sQuery(id+"F0.wireOp",EDGE,"E1.right")])]});
            var Q1;
            Q1=makeQuery(id+"F1.opExtrude","SWEPT_EDGE",EDGE,{"disambiguationData":[OSD([sQuery(id+"F0.wireOp",EDGE,"E0.2"),sQuery(id+"F0.wireOp",EDGE,"E1.bottom"),sQuery(id+"F0.wireOp",EDGE,"E0.0"),sQuery(id+"F0.wireOp",EDGE,"E2")])]});
            var Q2;
            Q2=makeQuery(id+"F1.opExtrude","SWEPT_EDGE",EDGE,{"disambiguationData":[OSD([sQuery(id+"F0.wireOp",EDGE,"E1.top"),sQuery(id+"F0.wireOp",EDGE,"E1.right")])]});
            var Q3;
            Q3=makeQuery(id+"F1.opExtrude","SWEPT_EDGE",EDGE,{"disambiguationData":[OSD([sQuery(id+"F0.wireOp",EDGE,"E0.1"),sQuery(id+"F0.wireOp",EDGE,"E1.top"),sQuery(id+"F0.wireOp",EDGE,"E0.0"),sQuery(id+"F0.wireOp",EDGE,"E7")])]});
            var Q4;
            Q4=makeQuery(id+"F1.opExtrude","SWEPT_EDGE",EDGE,{"disambiguationData":[OSD([sQuery(id+"F0.wireOp",EDGE,"E2"),sQuery(id+"F0.wireOp",EDGE,"E3")])]});
            var Q5;
            Q5=makeQuery(id+"F1.opExtrude","SWEPT_EDGE",EDGE,{"disambiguationData":[OSD([sQuery(id+"F0.wireOp",EDGE,"E3"),sQuery(id+"F0.wireOp",EDGE,"E4")])]});
            var Q6;
            Q6=makeQuery(id+"F1.opExtrude","SWEPT_EDGE",EDGE,{"disambiguationData":[OSD([sQuery(id+"F0.wireOp",EDGE,"E0.1"),sQuery(id+"F0.wireOp",EDGE,"E0.2"),sQuery(id+"F0.wireOp",EDGE,"E4"),sQuery(id+"F0.wireOp",EDGE,"E5")])]});
            var Q7;
            Q7=makeQuery(id+"F1.opExtrude","SWEPT_EDGE",EDGE,{"disambiguationData":[OSD([sQuery(id+"F0.wireOp",EDGE,"E5"),sQuery(id+"F0.wireOp",EDGE,"E6")])]});
            var Q8;
            Q8=makeQuery(id+"F1.opExtrude","SWEPT_EDGE",EDGE,{"disambiguationData":[OSD([sQuery(id+"F0.wireOp",EDGE,"E6"),sQuery(id+"F0.wireOp",EDGE,"E7")])]});
            fillet(context, id + "F20", {"entities" : qUnion([Q0, Q1, Q2, Q3, Q4, Q5, Q6, Q7, Q8]), "radius" : 3 * mm, "tangentPropagation" : true, "allowEdgeOverflow" : false});
        }
        {
            var Q0;
            Q0=makeQuery(id+"F1.opExtrude","SWEPT_EDGE",EDGE,{"disambiguationData":[OSD([sQuery(id+"F0.wireOp",EDGE,"E8.7"),sQuery(id+"F0.wireOp",EDGE,"E8.8")])]});
            var Q1;
            Q1=makeQuery(id+"F1.opExtrude","SWEPT_EDGE",EDGE,{"disambiguationData":[OSD([sQuery(id+"F0.wireOp",EDGE,"E8.4"),sQuery(id+"F0.wireOp",EDGE,"E8.8")])]});
            var Q2;
            Q2=makeQuery(id+"F1.opExtrude","SWEPT_EDGE",EDGE,{"disambiguationData":[OSD([sQuery(id+"F0.wireOp",EDGE,"E8.3"),sQuery(id+"F0.wireOp",EDGE,"E8.4")])]});
            var Q3;
            Q3=makeQuery(id+"F1.opExtrude","SWEPT_EDGE",EDGE,{"disambiguationData":[OSD([sQuery(id+"F0.wireOp",EDGE,"E8.1"),sQuery(id+"F0.wireOp",EDGE,"E8.3")])]});
            var Q4;
            Q4=makeQuery(id+"F1.opExtrude","SWEPT_EDGE",EDGE,{"disambiguationData":[OSD([sQuery(id+"F0.wireOp",EDGE,"E8.0"),sQuery(id+"F0.wireOp",EDGE,"E8.1")])]});
            var Q5;
            Q5=makeQuery(id+"F1.opExtrude","SWEPT_EDGE",EDGE,{"disambiguationData":[OSD([sQuery(id+"F0.wireOp",EDGE,"E8.0"),sQuery(id+"F0.wireOp",EDGE,"E8.2")])]});
            var Q6;
            Q6=makeQuery(id+"F1.opExtrude","SWEPT_EDGE",EDGE,{"disambiguationData":[OSD([sQuery(id+"F0.wireOp",EDGE,"E8.2"),sQuery(id+"F0.wireOp",EDGE,"E8.5")])]});
            var Q7;
            Q7=makeQuery(id+"F1.opExtrude","SWEPT_EDGE",EDGE,{"disambiguationData":[OSD([sQuery(id+"F0.wireOp",EDGE,"E8.5"),sQuery(id+"F0.wireOp",EDGE,"E8.6")])]});
            var Q8;
            Q8=makeQuery(id+"F1.opExtrude","SWEPT_EDGE",EDGE,{"disambiguationData":[OSD([sQuery(id+"F0.wireOp",EDGE,"E8.6"),sQuery(id+"F0.wireOp",EDGE,"E8.7")])]});
            fillet(context, id + "F21", {"entities" : qUnion([Q0, Q1, Q2, Q3, Q4, Q5, Q6, Q7, Q8]), "radius" : 3 * mm, "tangentPropagation" : true, "allowEdgeOverflow" : false});
        }
        {
            var Q0;
            Q0=qCreatedBy(makeId("Top.planeOp"),FACE);
            var sketch = newSketch(context, id + "F22", { "sketchPlane" : qUnion([Q0])});
            skLineSegment(sketch, "E25.bottom", {"start": v(48.71, 57.8) * mm, "end": v(72.71, 57.8) * mm});
            skLineSegment(sketch, "E25.top", {"start": v(48.71, 45.8) * mm, "end": v(72.71, 45.8) * mm});
            skLineSegment(sketch, "E25.left", {"start": v(48.71, 57.8) * mm, "end": v(48.71, 45.8) * mm});
            skLineSegment(sketch, "E25.right", {"start": v(72.71, 57.8) * mm, "end": v(72.71, 45.8) * mm});
            skLineSegment(sketch, "E26", {"start": v(66.71, 57.8) * mm, "end": v(66.71, 45.8) * mm});
            skSolve(sketch);
        }
        {
            var Q0;
            {var subQ0=sQuery(id+"F22.wireOp",EDGE,"E25.left");Q0=makeQuery(id+"F22.imprint","IMPRINT",FACE,{"disambiguationData":[TD([[makeQuery(id+"F22.imprint","IMPRINT",EDGE,{"derivedFrom":subQ0}),1.0]])]});}
            var Q1;
            {var subQ0=sQuery(id+"F22.wireOp",EDGE,"E25.right");Q1=makeQuery(id+"F22.imprint","IMPRINT",FACE,{"disambiguationData":[TD([[makeQuery(id+"F22.imprint","IMPRINT",EDGE,{"derivedFrom":subQ0}),-1.0]])]});}
            extrude(context, id + "F23", {"entities" : qUnion([Q0, Q1]), "depth" : 3 * mm, "offsetDistance" : 25 * mm});
        }
        {
            var Q0;
            {var subQ0=sQuery(id+"F22.wireOp",EDGE,"E25.right");Q0=makeQuery(id+"F22.imprint","IMPRINT",FACE,{"disambiguationData":[TD([[makeQuery(id+"F22.imprint","IMPRINT",EDGE,{"derivedFrom":subQ0}),-1.0]])]});}
            extrude(context, id + "F24", {"entities" : qUnion([Q0]), "operationType" : NewBodyOperationType.ADD, "depth" : 36 * mm, "offsetDistance" : 25 * mm});
        }
        {
            var Q0;
            Q0 = qSketchRegion(id + "F22", true);
            extrude(context, id + "F25", {"entities" : qUnion([Q0]), "operationType" : NewBodyOperationType.ADD, "depth" : 39 * mm, "offsetDistance" : 25 * mm, "hasSecondDirection" : true, "secondDirectionOppositeDirection" : false, "secondDirectionDepth" : 36 * mm});
        }
        {
            var Q0;
            Q0=makeQuery(id+"F24.boolean.opBoolean","INTERSECT",EDGE,{"derivedFrom":[makeQuery(id+"F23.opExtrude","CAP_FACE",FACE,{"disambiguationData":[OSD([sQuery(id+"F22.wireOp",EDGE,"E25.bottom"),sQuery(id+"F22.wireOp",EDGE,"E25.top"),sQuery(id+"F22.wireOp",EDGE,"E25.left"),sQuery(id+"F22.wireOp",EDGE,"E25.right")])],"isStart":false}),makeQuery(id+"F24.opExtrude","SWEPT_FACE",FACE,{"disambiguationData":[OSD([sQuery(id+"F22.wireOp",EDGE,"E26")])]})]});
            var Q1;
            Q1=makeQuery(id+"F24.opExtrude","CAP_EDGE",EDGE,{"disambiguationData":[OSD([sQuery(id+"F22.wireOp",EDGE,"E26")])],"isStart":false});
            var Q2;
            Q2=makeQuery(id+"F25.opExtrude","CAP_EDGE",EDGE,{"disambiguationData":[OSD([sQuery(id+"F22.wireOp",EDGE,"E25.right")])],"isStart":false});
            var Q3;
            Q3=makeQuery(id+"F23.opExtrude","CAP_EDGE",EDGE,{"disambiguationData":[OSD([sQuery(id+"F22.wireOp",EDGE,"E25.right")])],"isStart":true});
            fillet(context, id + "F26", {"entities" : qUnion([Q0, Q1, Q2, Q3]), "radius" : 5 * mm, "tangentPropagation" : true, "allowEdgeOverflow" : false});
        }
        {
            var Q0;
            Q0=makeQuery(id+"F25.opExtrude","CAP_FACE",FACE,{"disambiguationData":[OSD([sQuery(id+"F22.wireOp",EDGE,"E25.bottom"),sQuery(id+"F22.wireOp",EDGE,"E25.top"),sQuery(id+"F22.wireOp",EDGE,"E25.left"),sQuery(id+"F22.wireOp",EDGE,"E25.right")])],"isStart":false});
            var sketch = newSketch(context, id + "F27", { "sketchPlane" : qUnion([Q0])});
            skCircle(sketch, "E27", {"center": v(58.21, 51.8) * mm, "radius": 1.4 * mm});
            skPoint(sketch, "E27.centerSnap0", {"position": v(58.21, 57.8) * mm});
            skPoint(sketch, "E27.centerSnap1", {"position": v(48.71, 51.8) * mm});
            skSolve(sketch);
        }
        {
            var Q0;
            Q0=makeQuery(id+"F27.imprint","IMPRINT",FACE,{"disambiguationData":[TD([[makeQuery(id+"F27.imprint","IMPRINT",EDGE,{"derivedFrom":sQuery(id+"F27.wireOp",EDGE,"E27")}),1.0]])]});
            extrude(context, id + "F28", {"entities" : qUnion([Q0]), "operationType" : NewBodyOperationType.REMOVE, "oppositeDirection" : true, "depth" : 54.3 * mm, "offsetDistance" : 25 * mm});
        }
    });
